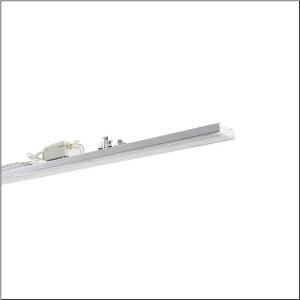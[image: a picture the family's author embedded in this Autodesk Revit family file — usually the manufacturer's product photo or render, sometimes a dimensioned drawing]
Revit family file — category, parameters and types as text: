
# Revit family: licross_11_recessed_mo_51te10dn495g
name_source: partatom
category: Lighting Fixtures
units: mm (PartAtom-declared; Revit-internal decimal feet)

## family parameters
Cut with Voids When Loaded = No
Host = Face
Light Source = No
Part Type = Normal
Room Calculation Point = No
Round Connector Dimension = Use Diameter
Shared = No

## types (1)
- --- (1 x LED, 9960 lm, 56.7 W, 4000K)
    Apparent Load = 57 VA
    CIE Flux Codes = 50 81 96 100 100
    Color Rendering = 80
    Color Temperature = 4000K
    Default Elevation = 1800 mm
    Description = Licross 11 Recessed MO, luminaire insert, of sheet steel, galvanised, coil coated, white, length: 1.500mm, width: 66mm, height: 67mm, LED rated luminous flux: 9.960lm, light colour: 840, SDCM (Standard Deviation of Colour Matching)MacAdam ≤ 2 SDCM (initial), control gear: DALI 2, with plug, 5-pole, with phase selection, mains connection: 220..240V, AC, 50/60Hz, rated input power: 57W, internal wiring halogen-free, primary optical cover: cover, of PMMA, light emission: direct distribution, primary light characteristic: symmetric, protection rating (complete): IP54, insulation class (complete): insulation class I (protective earthing), certification: CE, ENEC, VDE, UKCA, protection symbol: D if used in an environment with non-conductive dust loads with corresponding accessories, impact resistance: IK06, permissible ambient temperature for indoor applications: -25..+35°C, corresponds to IFS (International Featured Standards) requirements for safety and quality in the food industry, reducing of maximum allowable ambient temperature of 5°C with ceiling mounting, LABS conformity tested according to VDMA 24364:2018-05, The light source and the operating device comply with the requirements of the Ecodesign Regulation (EU) 2019/2020 and are replaceable in accordance with this regulation, packaging unit: 1 piece
    Height = 58 mm
    Lamp = 1 x LED
    Lamp Light Flux = 9960 lm
    Lamp Power = 56.7 W
    Lamp count = 1
    Length = 1500 mm
    Luminous efficacy = 176 lm/W
    Manufacturer = Siteco
    ModVariant = No
    Model = 51TE10DN495G
    Mounting Place = Ceiling
    Mounting Type = Pendant
    Number of Poles = 1
    OnlyDefault = Yes
    Power Factor = 1
    Product Name = Licross 11 Recessed MO
    Product group = luminaire insert | ceiling pendant
    ProductGroupID = 901
    Protection Class = Protection class I
    Protection Degree = IP 54
    RLX_Detail_Level = 1
    RLX_Emergency_Light_Flux = 0 lm
    RLX_Emergency_Type = 0
    RLX_Emergency_Type_DB = No
    RlxData = <blob elided: 24573 chars, md5=1a76dea1>
    Socket = socket
    Standby Power = 0 W
    System Light Flux = 9960 lm
    System Power = 57 W
    Type Comments = factory setting: luminous flux: 100 % | dim-lin: 254 | 378 mA
    Type Image = l_1296930.jpg
    URL = http://relux.com
    VarID = @adj_102953
    Voltage = 0 V
    Weight = 0.00 kg
    Width = 66 mm

## geometry (parser evidence)
native form markers: Blend x4, Sweep x11
no freeform markers — native parametric forms only
